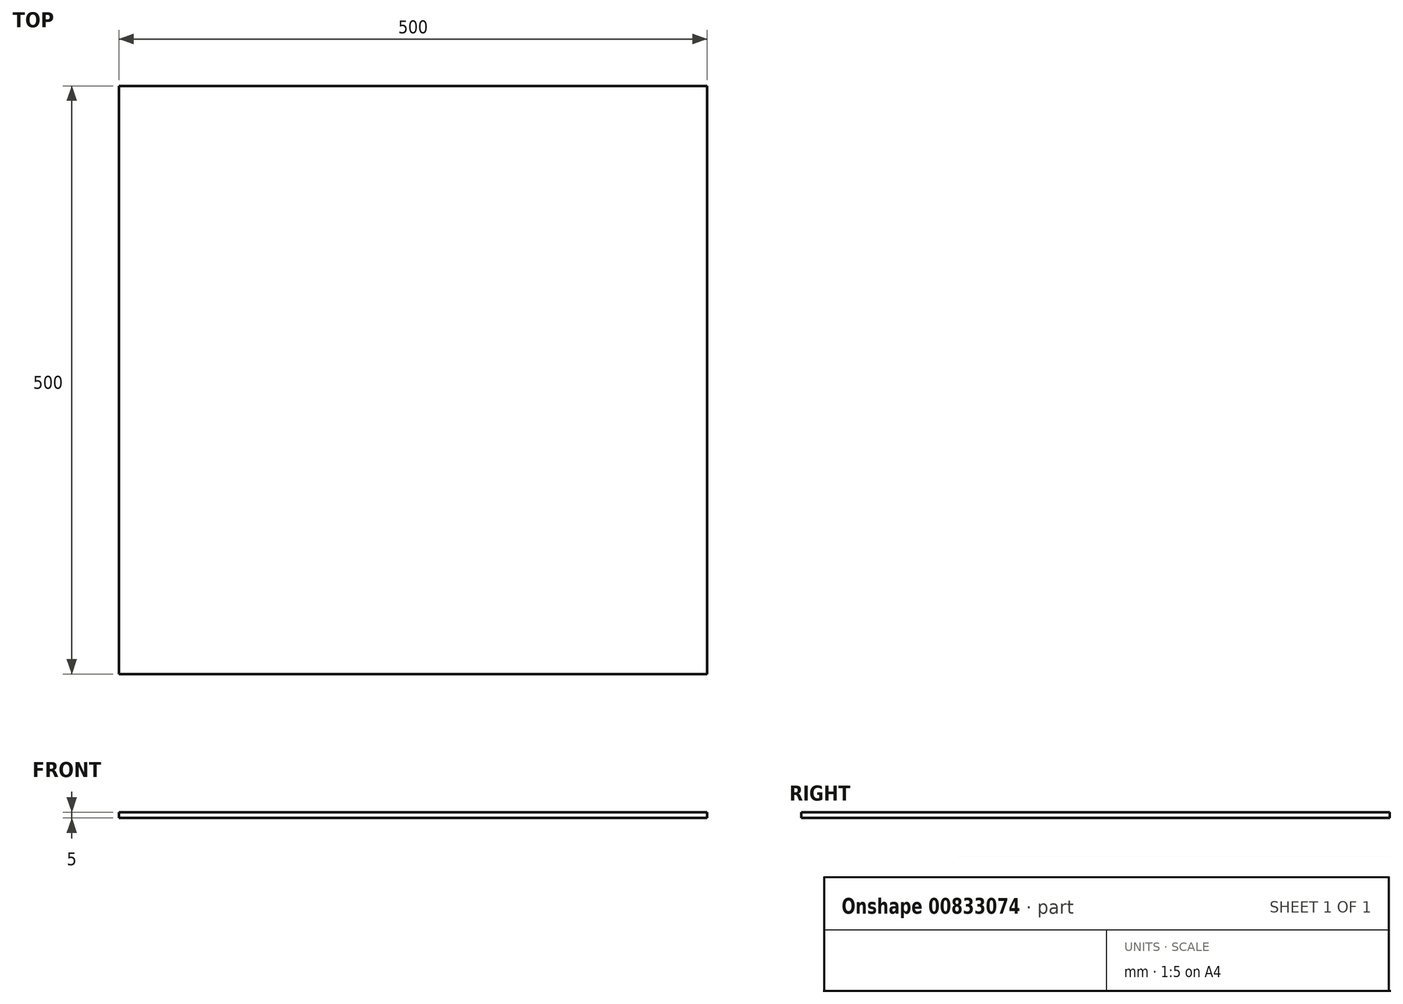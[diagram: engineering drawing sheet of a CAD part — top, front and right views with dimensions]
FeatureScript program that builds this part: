
annotation { "Feature Type Name" : "Feature", "Feature Type Description" : "" }
export const myFeature = defineFeature(function(context is Context, id is Id, definition is map)
    precondition{}
    {
        {
            var Q0;
            Q0=qCreatedBy(makeId("Top.planeOp"),FACE);
            var sketch = newSketch(context, id + "F0", { "sketchPlane" : qUnion([Q0])});
            skLineSegment(sketch, "E0.bottom", {"start": v(-254.47, 305.92) * mm, "end": v(245.53, 305.92) * mm});
            skLineSegment(sketch, "E0.top", {"start": v(-254.47, -194.08) * mm, "end": v(245.53, -194.08) * mm});
            skLineSegment(sketch, "E0.left", {"start": v(-254.47, 305.92) * mm, "end": v(-254.47, -194.08) * mm});
            skLineSegment(sketch, "E0.right", {"start": v(245.53, 305.92) * mm, "end": v(245.53, -194.08) * mm});
            skSolve(sketch);
        }
        {
            var Q0;
            Q0=makeQuery(id+"F0.imprint","IMPRINT",FACE,{"disambiguationData":[TD([[makeQuery(id+"F0.imprint","IMPRINT",EDGE,{"derivedFrom":sQuery(id+"F0.wireOp",EDGE,"E0.bottom")}),-1.0]])]});
            extrude(context, id + "F1", {"entities" : qUnion([Q0]), "depth" : 4 * mm, "offsetDistance" : 25 * mm});
        }
        {
            var Q0;
            Q0=makeQuery(id+"F1.opExtrude","CAP_FACE",FACE,{"disambiguationData":[OSD([sQuery(id+"F0.wireOp",EDGE,"E0.bottom"),sQuery(id+"F0.wireOp",EDGE,"E0.top"),sQuery(id+"F0.wireOp",EDGE,"E0.left"),sQuery(id+"F0.wireOp",EDGE,"E0.right")])],"isStart":false});
            extrude(context, id + "F2", {"entities" : qUnion([Q0]), "operationType" : NewBodyOperationType.ADD, "depth" : .5 * mm, "offsetDistance" : 25 * mm});
        }
        {
            var Q0;
            Q0=makeQuery(id+"F2.opExtrude","CAP_FACE",FACE,{"disambiguationData":[OSD([sQuery(id+"F0.wireOp",EDGE,"E0.bottom"),sQuery(id+"F0.wireOp",EDGE,"E0.top"),sQuery(id+"F0.wireOp",EDGE,"E0.left"),sQuery(id+"F0.wireOp",EDGE,"E0.right")])],"isStart":false});
            extrude(context, id + "F3", {"entities" : qUnion([Q0]), "operationType" : NewBodyOperationType.ADD, "depth" : .5 * mm, "offsetDistance" : 25 * mm});
        }
    });
